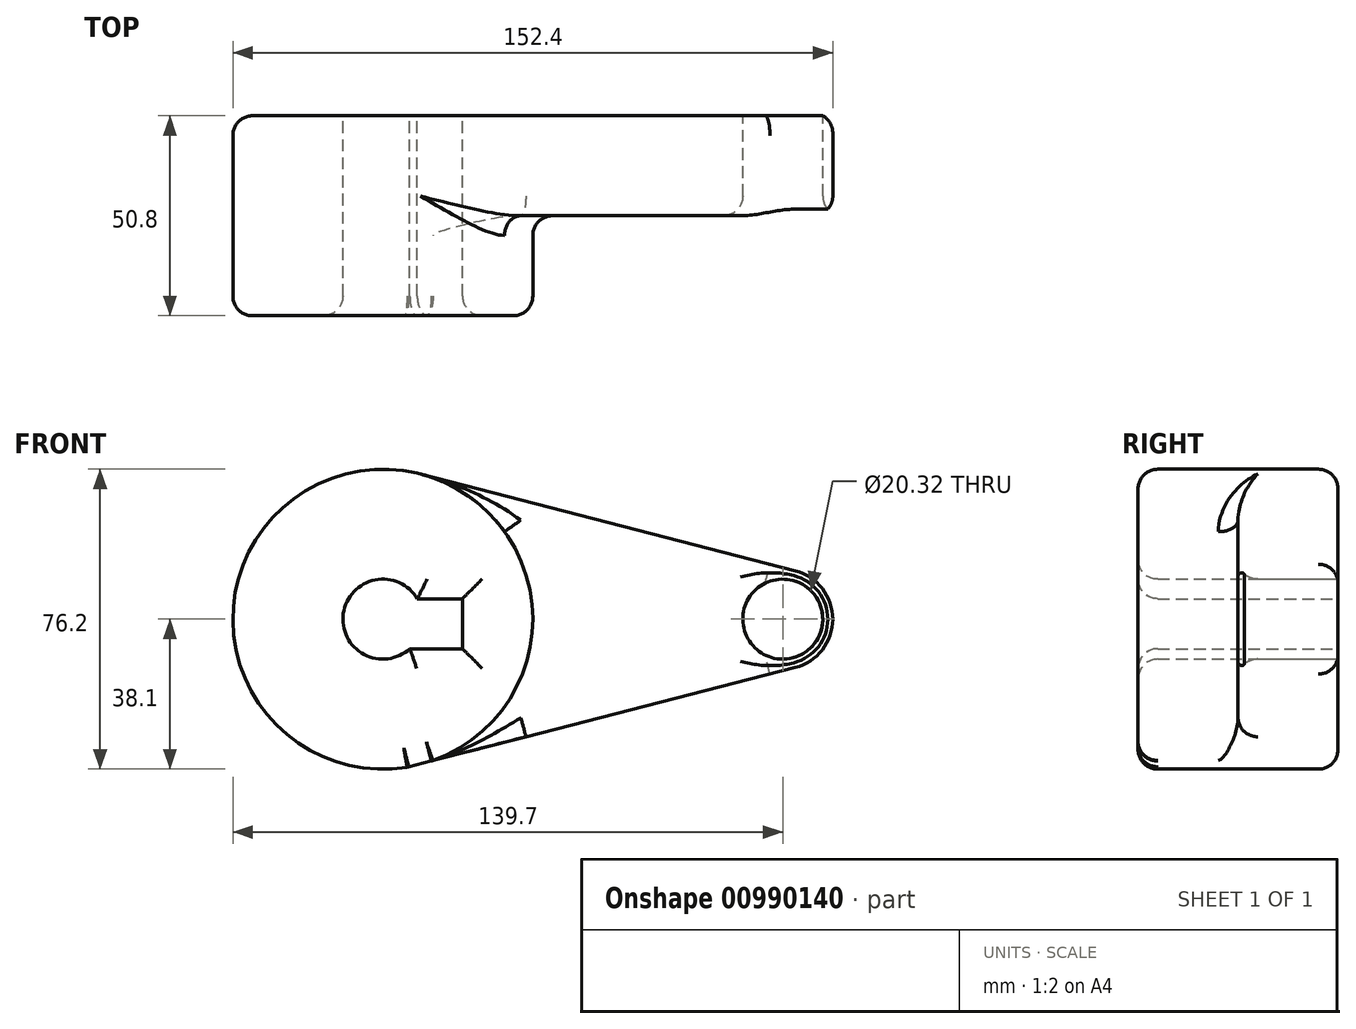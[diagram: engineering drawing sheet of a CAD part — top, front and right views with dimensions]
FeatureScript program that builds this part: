
annotation { "Feature Type Name" : "Feature", "Feature Type Description" : "" }
export const myFeature = defineFeature(function(context is Context, id is Id, definition is map)
    precondition{}
    {
        {
            var Q0;
            Q0=qCreatedBy(makeId("Front.planeOp"),FACE);
            var sketch = newSketch(context, id + "F0", { "sketchPlane" : qUnion([Q0])});
            skCircle(sketch, "E0", {"center": v(0, 0) * mm, "radius": 38.1 * mm});
            skCircle(sketch, "E1", {"center": v(101.6, 0) * mm, "radius": 12.7 * mm});
            skLineSegment(sketch, "E2", {"start": v(9.52, 36.9) * mm, "end": v(104.78, 12.3) * mm});
            skLineSegment(sketch, "E3", {"start": v(6.37, -37.56) * mm, "end": v(104.76, -12.3) * mm});
            skCircle(sketch, "E4", {"center": v(0, 0) * mm, "radius": 10.16 * mm});
            skCircle(sketch, "E5", {"center": v(101.6, 0) * mm, "radius": 10.16 * mm});
            skLineSegment(sketch, "E6.bottom", {"start": v(-22.96, 5.2) * mm, "end": v(20.22, 5.2) * mm});
            skLineSegment(sketch, "E6.top", {"start": v(-22.96, -7.5) * mm, "end": v(20.22, -7.5) * mm});
            skLineSegment(sketch, "E6.left", {"start": v(-22.96, 5.2) * mm, "end": v(-22.96, -7.5) * mm});
            skLineSegment(sketch, "E6.right", {"start": v(20.22, 5.2) * mm, "end": v(20.22, -7.5) * mm});
            skSolve(sketch);
        }
        {
            var Q0;
            {var subQ4=sQuery(id+"F0.wireOp",EDGE,"E6.left");Q0=makeQuery(id+"F0.imprint","IMPRINT",FACE,{"disambiguationData":[TD([[makeQuery(id+"F0.imprint","IMPRINT",EDGE,{"derivedFrom":subQ4}),-1.0]])]});}
            var Q1;
            {var subQ0=sQuery(id+"F0.wireOp",EDGE,"E2");Q1=makeQuery(id+"F0.imprint","IMPRINT",FACE,{"disambiguationData":[TD([[makeQuery(id+"F0.imprint","IMPRINT",EDGE,{"derivedFrom":subQ0}),-1.0]])]});}
            var Q2;
            Q2=makeQuery(id+"F0.imprint","IMPRINT",FACE,{"disambiguationData":[TD([[makeQuery(id+"F0.imprint","IMPRINT",EDGE,{"derivedFrom":sQuery(id+"F0.wireOp",EDGE,"E5")}),-1.0]])]});
            var Q3;
            {var subQ5=sQuery(id+"F0.wireOp",EDGE,"E6.left");Q3=makeQuery(id+"F0.imprint","IMPRINT",FACE,{"disambiguationData":[TD([[makeQuery(id+"F0.imprint","IMPRINT",EDGE,{"derivedFrom":subQ5}),1.0]])]});}
            extrude(context, id + "F1", {"entities" : qUnion([Q0, Q1, Q2, Q3]), "depth" : 25.4 * mm, "offsetDistance" : 25.4 * mm});
        }
        {
            var Q0;
            {var subQ4=sQuery(id+"F0.wireOp",EDGE,"E6.left");Q0=makeQuery(id+"F0.imprint","IMPRINT",FACE,{"disambiguationData":[TD([[makeQuery(id+"F0.imprint","IMPRINT",EDGE,{"derivedFrom":subQ4}),-1.0]])]});}
            var Q1;
            {var subQ5=sQuery(id+"F0.wireOp",EDGE,"E6.left");Q1=makeQuery(id+"F0.imprint","IMPRINT",FACE,{"disambiguationData":[TD([[makeQuery(id+"F0.imprint","IMPRINT",EDGE,{"derivedFrom":subQ5}),1.0]])]});}
            extrude(context, id + "F2", {"entities" : qUnion([Q0, Q1]), "operationType" : NewBodyOperationType.ADD, "depth" : 25.4 * mm, "offsetDistance" : 25.4 * mm});
        }
        {
            var Q0;
            {var subQ4=sQuery(id+"F0.wireOp",EDGE,"E6.left");Q0=makeQuery(id+"F0.imprint","IMPRINT",FACE,{"disambiguationData":[TD([[makeQuery(id+"F0.imprint","IMPRINT",EDGE,{"derivedFrom":subQ4}),-1.0]])]});}
            var Q1;
            {var subQ5=sQuery(id+"F0.wireOp",EDGE,"E6.left");Q1=makeQuery(id+"F0.imprint","IMPRINT",FACE,{"disambiguationData":[TD([[makeQuery(id+"F0.imprint","IMPRINT",EDGE,{"derivedFrom":subQ5}),1.0]])]});}
            extrude(context, id + "F3", {"entities" : qUnion([Q0, Q1]), "operationType" : NewBodyOperationType.ADD, "depth" : 50.8 * mm, "offsetDistance" : 25.4 * mm});
        }
        {
            var Q0;
            Q0=makeQuery(id+"F1.opExtrude","CAP_FACE",FACE,{"disambiguationData":[OSD([sQuery(id+"F0.wireOp",EDGE,"E0"),sQuery(id+"F0.wireOp",EDGE,"E1"),sQuery(id+"F0.wireOp",EDGE,"E2"),sQuery(id+"F0.wireOp",EDGE,"E3"),sQuery(id+"F0.wireOp",EDGE,"E4"),sQuery(id+"F0.wireOp",EDGE,"E5"),sQuery(id+"F0.wireOp",EDGE,"E6.bottom"),sQuery(id+"F0.wireOp",EDGE,"E6.top"),sQuery(id+"F0.wireOp",EDGE,"E6.right")])],"isStart":false});
            var Q1;
            {var subQ0=sQuery(id+"F0.wireOp",EDGE,"E3");Q1=makeQuery(id+"F3.boolean.opBoolean","MERGE",FACE,{"derivedFrom":[makeQuery(id+"F1.opExtrude","SWEPT_FACE",FACE,{"disambiguationData":[OSD([subQ0])]}),makeQuery(id+"F3.opExtrude","SWEPT_FACE",FACE,{"disambiguationData":[OSD([subQ0])]})]});}
            fillet(context, id + "F4", {"entities" : qUnion([Q0, Q1]), "radius" : 5 * mm, "tangentPropagation" : true, "allowEdgeOverflow" : false});
        }
        {
            var Q0;
            Q0=makeQuery(id+"F3.opExtrude","CAP_FACE",FACE,{"disambiguationData":[OSD([sQuery(id+"F0.wireOp",EDGE,"E0"),sQuery(id+"F0.wireOp",EDGE,"E3"),sQuery(id+"F0.wireOp",EDGE,"E4"),sQuery(id+"F0.wireOp",EDGE,"E6.bottom"),sQuery(id+"F0.wireOp",EDGE,"E6.top"),sQuery(id+"F0.wireOp",EDGE,"E6.right")])],"isStart":false});
            var Q1;
            {var subQ0=sQuery(id+"F0.wireOp",EDGE,"E0");Q1=makeQuery(id+"F3.boolean.opBoolean","MERGE",FACE,{"derivedFrom":[makeQuery(id+"F1.opExtrude","SWEPT_FACE",FACE,{"disambiguationData":[OSD([subQ0])]}),makeQuery(id+"F3.opExtrude","SWEPT_FACE",FACE,{"disambiguationData":[OSD([subQ0])]})]});}
            fillet(context, id + "F5", {"entities" : qUnion([Q0, Q1]), "radius" : 5 * mm, "tangentPropagation" : true, "allowEdgeOverflow" : false});
        }
    });
